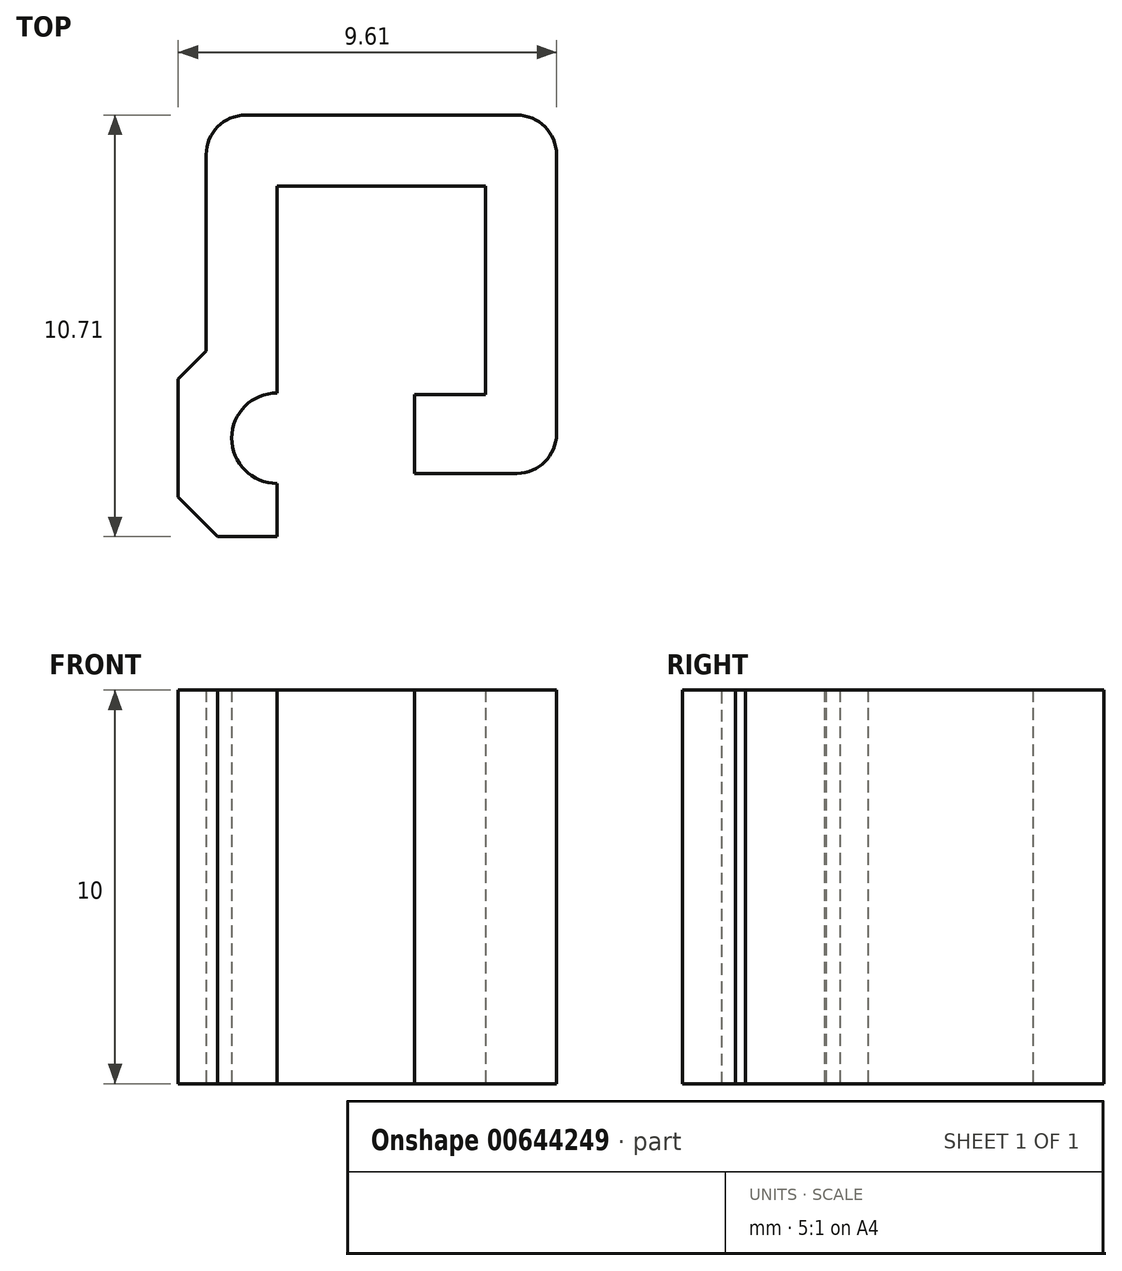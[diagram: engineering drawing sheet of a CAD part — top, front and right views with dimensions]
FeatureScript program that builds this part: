
annotation { "Feature Type Name" : "Feature", "Feature Type Description" : "" }
export const myFeature = defineFeature(function(context is Context, id is Id, definition is map)
    precondition{}
    {
        {
            var Q0;
            Q0=qCreatedBy(makeId("Top.planeOp"),FACE);
            var sketch = newSketch(context, id + "F0", { "sketchPlane" : qUnion([Q0])});
            skLineSegment(sketch, "E0", {"start": v(0, 0) * mm, "end": v(0, 8.9) * mm});
            skLineSegment(sketch, "E1", {"start": v(0, 8.9) * mm, "end": v(5.3, 8.9) * mm});
            skLineSegment(sketch, "E2", {"start": v(5.3, 8.9) * mm, "end": v(5.3, 3.6) * mm});
            skLineSegment(sketch, "E3", {"start": v(5.3, 3.6) * mm, "end": v(3.5, 3.6) * mm});
            skLineSegment(sketch, "E4", {"start": v(3.5, 3.6) * mm, "end": v(3.5, 1.6) * mm});
            skLineSegment(sketch, "E5", {"start": v(3.5, 1.6) * mm, "end": v(7.1, 1.6) * mm});
            skLineSegment(sketch, "E6", {"start": v(7.1, 1.6) * mm, "end": v(7.1, 10.7) * mm});
            skLineSegment(sketch, "E7", {"start": v(7.1, 10.7) * mm, "end": v(-1.8, 10.7) * mm});
            skLineSegment(sketch, "E8", {"start": v(-1.8, 10.7) * mm, "end": v(-1.8, 4.7) * mm});
            skLineSegment(sketch, "E9", {"start": v(-1.8, 4.7) * mm, "end": v(-2.5, 4) * mm});
            skLineSegment(sketch, "E10", {"start": v(-2.5, 4) * mm, "end": v(-2.5, 0) * mm});
            skLineSegment(sketch, "E11", {"start": v(-2.5, 0) * mm, "end": v(0, 0) * mm});
            skCircle(sketch, "E12", {"center": v(0, 2.5) * mm, "radius": 1.15 * mm});
            skSolve(sketch);
        }
        {
            var Q0;
            {var subQ4=sQuery(id+"F0.wireOp",EDGE,"E1");Q0=makeQuery(id+"F0.imprint","IMPRINT",FACE,{"disambiguationData":[TD([[makeQuery(id+"F0.imprint","IMPRINT",EDGE,{"derivedFrom":subQ4}),1.0]])]});}
            extrude(context, id + "F1", {"entities" : qUnion([Q0]), "depth" : 10 * mm, "offsetDistance" : 25 * mm});
        }
        {
            var Q0;
            Q0=makeQuery(id+"F1.opExtrude","SWEPT_EDGE",EDGE,{"disambiguationData":[OSD([sQuery(id+"F0.wireOp",EDGE,"E10"),sQuery(id+"F0.wireOp",EDGE,"E11")])]});
            chamfer(context, id + "F2", {"entities" : qUnion([Q0]), "width" : 1 * mm, "tangentPropagation" : true});
        }
        {
            var Q0;
            Q0=makeQuery(id+"F1.opExtrude","SWEPT_EDGE",EDGE,{"disambiguationData":[OSD([sQuery(id+"F0.wireOp",EDGE,"E5"),sQuery(id+"F0.wireOp",EDGE,"E6")])]});
            var Q1;
            Q1=makeQuery(id+"F1.opExtrude","SWEPT_EDGE",EDGE,{"disambiguationData":[OSD([sQuery(id+"F0.wireOp",EDGE,"E6"),sQuery(id+"F0.wireOp",EDGE,"E7")])]});
            var Q2;
            Q2=makeQuery(id+"F1.opExtrude","SWEPT_EDGE",EDGE,{"disambiguationData":[OSD([sQuery(id+"F0.wireOp",EDGE,"E7"),sQuery(id+"F0.wireOp",EDGE,"E8")])]});
            fillet(context, id + "F3", {"entities" : qUnion([Q0, Q1, Q2]), "tangentPropagation" : true, "radius" : 1 * mm, "defaultsChanged" : true, "vertexSettings" : [], "allowEdgeOverflow" : false});
        }
    });
